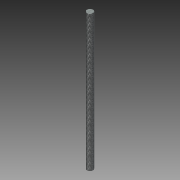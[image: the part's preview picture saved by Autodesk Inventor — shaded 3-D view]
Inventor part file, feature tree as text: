
AUTODESK INVENTOR PART (.ipt)
format: ipt  version: 2012 (Build 160160000, 160)  size: 68,096 bytes
history: native  units: mm
features: extrude x1, thread x1, sketch x1
ambient origin geometry x8: Origin, YZ Plane, XZ Plane, XY Plane, X Axis, Y Axis, Z Axis, Center Point
bodies: Solid1 (feature_tree)
feature tree (3):
  extrude  "Extrusion1"  Depth=184.0mm TaperAngle=0.0deg
  thread  "Thread1"  [1 undecoded]
  sketch  "Sketch1"  dims[d0=8.0mm d1=184.0mm d2=0.0mm d3=10.0mm d4=0.0mm]
note: 1 required parameter value undecoded (feature->parameter linkage not recoverable at this tier; creation-order binding heuristic only, values carry confidence <= 0.55)
